# Revit family: HL_Трап для балконов и террас_HL81GH
name_source: partatom
category: Instalační zařizovací předměty
revit_build: Autodesk Revit 2016 (Build: 20151007_0715(x64)
units: mm (PartAtom-declared; Revit-internal decimal feet)

## family parameters
Bod výpočtu místnosti = Ano
Kóta kulaté spojky = Použít průměr
Nadpis OmniClass = Deck Waste Water Drains
Ořezat dutým tvarem při načtení = Ne
Sdílené = Ne
Typ součásti = Normální
Vždy vertikální = Ano
Založené na pracovní rovině = Ne
Číslo OmniClass = 23.70.50.21.24.14

## types (1)
- HL_Трап для балконов и террас_HL81GH
    EAN = 9003076003372
    Klíčová poznámka = HL81GH
    Komentáře k typům = Трап для балконов и террас DN50/75 поворотный с битумным полотном,с морозоустойчивой запахозапирающей заслонкой, 150х150мм/137х137мм чугун
    Model = HL81GH
    Popis = Трап для балконов и террас
    Připojení CW = Ne
    Připojení HW = Ne
    Připojení odpadu = Ano
    Připojení ventilace = Ne
    URL = http://www.hutterer-lechner.com
    Výrobce = HL Hutterer & Lechner GmbH
    ВЕС = 3,114 kg
    МАКСИМАЛЬНАЯ НАГРУЗКА КЛАССА = A - 1,5 t (aussen)
    МАТЕРИАЛ = PP / PE
    НАСАДКА = 34-73mm/150x150mm Guss
    ПРОИЗВОДИТЕЛЬНОСТЬ = 0,80 l/s
    РАЗМЕР = DN50/75
    РЕШЁТКА = Gusseisen 137x137mm

## geometry (parser evidence)
native form markers: Blend x8, Sweep x27
no freeform markers — native parametric forms only
